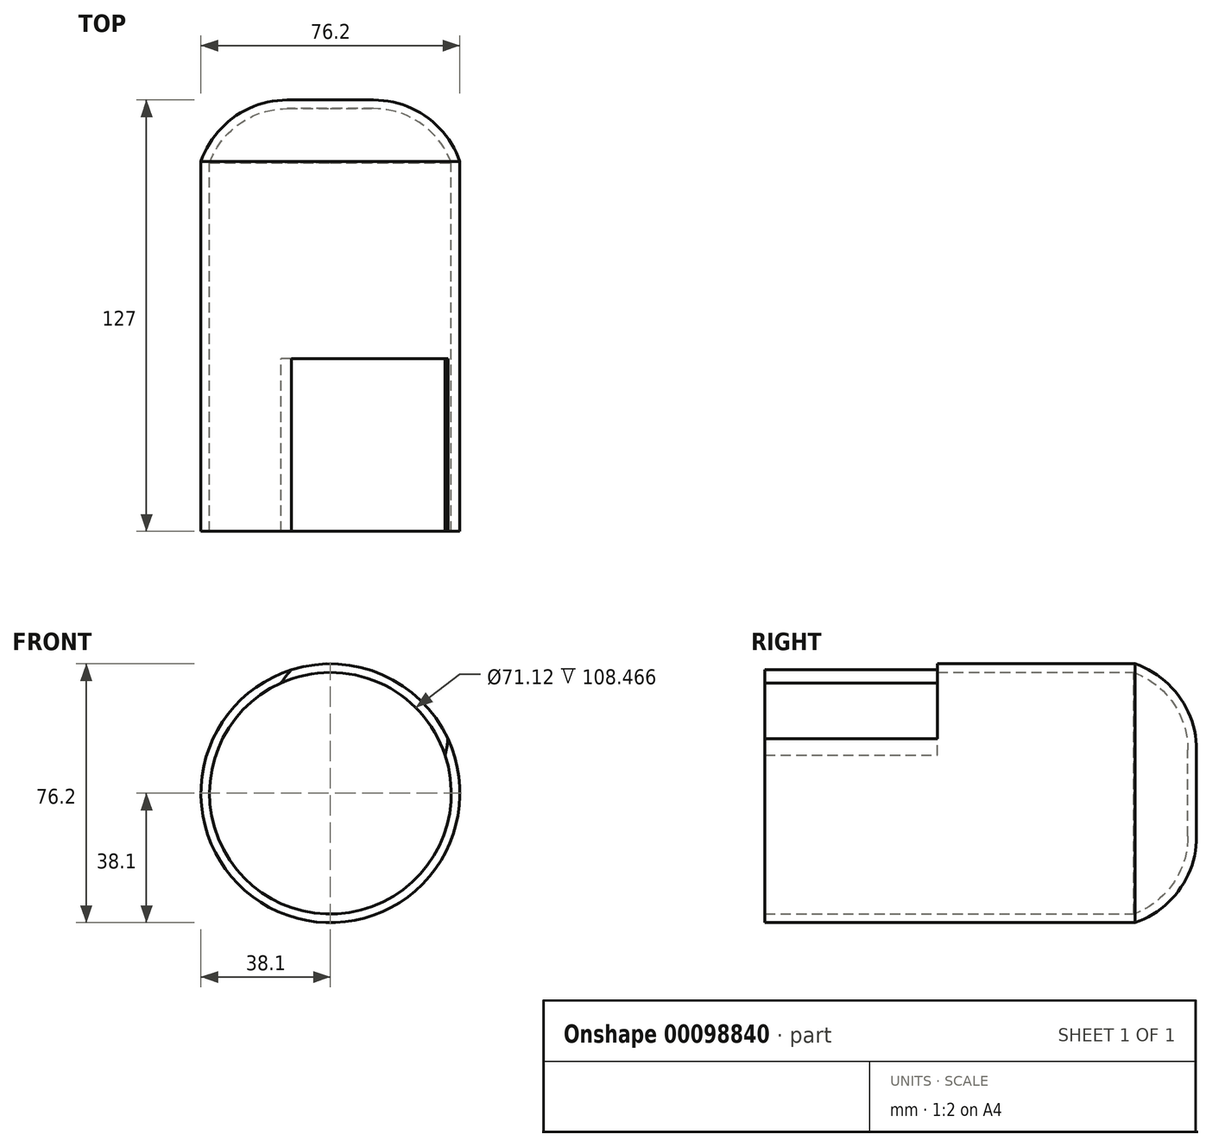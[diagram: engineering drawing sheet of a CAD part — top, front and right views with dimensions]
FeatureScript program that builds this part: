
annotation { "Feature Type Name" : "Feature", "Feature Type Description" : "" }
export const myFeature = defineFeature(function(context is Context, id is Id, definition is map)
    precondition{}
    {
        {
            var Q0;
            Q0=qCreatedBy(makeId("Front.planeOp"),FACE);
            var sketch = newSketch(context, id + "F0", { "sketchPlane" : qUnion([Q0])});
            skCircle(sketch, "E0", {"center": v(0, 0) * mm, "radius": 38.1 * mm});
            skSolve(sketch);
        }
        {
            var Q0;
            Q0=makeQuery(id+"F0.imprint","IMPRINT",FACE,{"disambiguationData":[TD([[makeQuery(id+"F0.imprint","IMPRINT",EDGE,{"derivedFrom":sQuery(id+"F0.wireOp",EDGE,"E0")}),1.0]])]});
            extrude(context, id + "F1", {"entities" : qUnion([Q0]), "depth" : 127 * mm});
        }
        {
            var Q0;
            Q0=qCreatedBy(makeId("Top.planeOp"),FACE);
            var sketch = newSketch(context, id + "F2", { "sketchPlane" : qUnion([Q0])});
            skLineSegment(sketch, "E1", {"start": v(0, 0) * mm, "end": v(-12.7, 0) * mm});
            skArc(sketch, "E2", {"start": v(-12.7, 0) * mm, "mid": v(-32.1, -8.28) * mm, "end": v(-39.55, -28.03) * mm});
            skLineSegment(sketch, "E3", {"start": v(-39.55, -28.03) * mm, "end": v(-68.36, -28.03) * mm});
            skLineSegment(sketch, "E4", {"start": v(-68.36, -28.03) * mm, "end": v(-68.36, 26.98) * mm});
            skLineSegment(sketch, "E5", {"start": v(-68.36, 26.98) * mm, "end": v(0, 26.98) * mm});
            skLineSegment(sketch, "E6", {"start": v(0, 26.98) * mm, "end": v(0, 0) * mm});
            skSolve(sketch);
        }
        {
            var Q0;
            Q0=makeQuery(id+"F2.imprint","IMPRINT",FACE,{"disambiguationData":[TD([[makeQuery(id+"F2.imprint","IMPRINT",EDGE,{"derivedFrom":sQuery(id+"F2.wireOp",EDGE,"E1")}),-1.0]])]});
            var Q1;
            Q1=sQuery(id+"F2.wireOp",EDGE,"E6");
            revolve(context, id + "F3", {"operationType" : NewBodyOperationType.REMOVE, "entities" : qUnion([Q0]), "axis" : qUnion([Q1]), "revolveType" : RevolveType.FULL, "oppositeDirection" : true});
        }
        {
            var Q0;
            Q0=qCreatedBy(makeId("Front.planeOp"),FACE);
            cPlane(context, id + "F4", {"entities" : qUnion([Q0]), "cplaneType" : CPlaneType.OFFSET, "offset" : 76.2 * mm, "width" : 152.4 * mm, "height" : 152.4 * mm});
        }
        {
            var Q0;
            Q0=qCreatedBy(id+"F4.planeOp",FACE);
            var sketch = newSketch(context, id + "F5", { "sketchPlane" : qUnion([Q0])});
            skCircle(sketch, "E7", {"center": v(7.96, 18.03) * mm, "radius": 26.7 * mm});
            skSolve(sketch);
        }
        {
            var Q0;
            Q0=makeQuery(id+"F1.opExtrude","CAP_FACE",FACE,{"disambiguationData":[OSD([sQuery(id+"F0.wireOp",EDGE,"E0")])],"isStart":false});
            shell(context, id + "F6", {"entities" : qUnion([Q0]), "thickness" : 2.54 * mm});
        }
        {
            var Q0;
            Q0=qCreatedBy(id+"F4.planeOp",FACE);
            cPlane(context, id + "F7", {"entities" : qUnion([Q0]), "cplaneType" : CPlaneType.OFFSET, "offset" : 50.8 * mm, "oppositeDirection" : true, "width" : 152.4 * mm, "height" : 152.4 * mm});
        }
        {
            var Q0;
            Q0=makeQuery(id+"F5.imprint","IMPRINT",FACE,{"disambiguationData":[TD([[makeQuery(id+"F5.imprint","IMPRINT",EDGE,{"derivedFrom":sQuery(id+"F5.wireOp",EDGE,"E7")}),1.0]])]});
            var Q1;
            Q1=sQuery(id+"F5.wireOp",EDGE,"E7");
            extrude(context, id + "F8", {"entities" : qUnion([Q0]), "operationType" : NewBodyOperationType.REMOVE, "surfaceEntities" : qUnion([Q1]), "depth" : 68.49 * mm});
        }
    });
